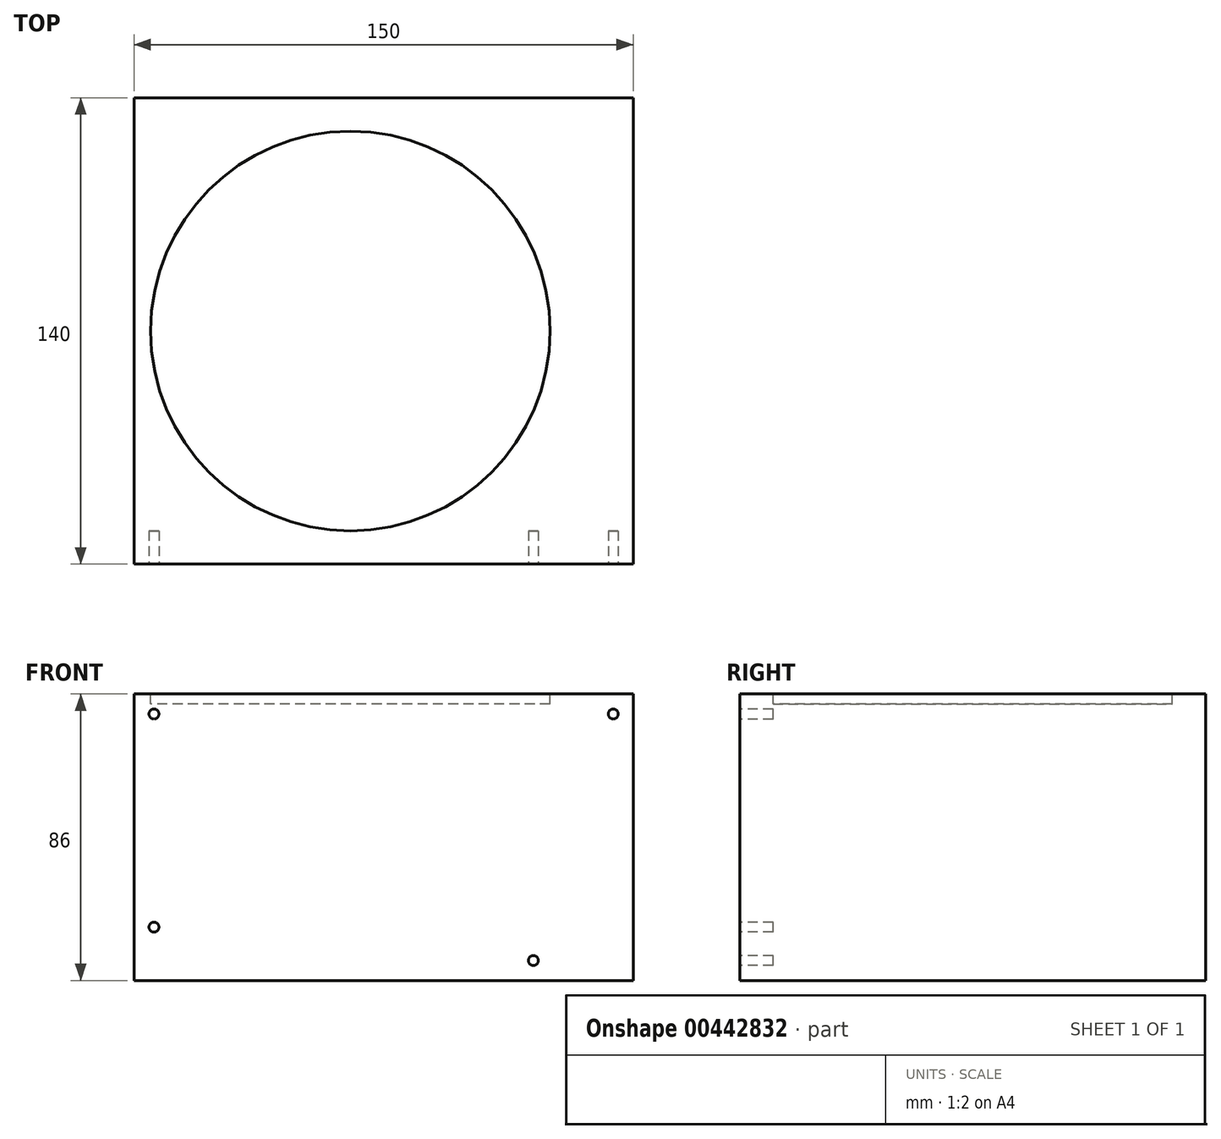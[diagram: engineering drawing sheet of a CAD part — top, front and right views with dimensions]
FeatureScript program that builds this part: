
annotation { "Feature Type Name" : "Feature", "Feature Type Description" : "" }
export const myFeature = defineFeature(function(context is Context, id is Id, definition is map)
    precondition{}
    {
        {
            var Q0;
            Q0=qCreatedBy(makeId("Top.planeOp"),FACE);
            var sketch = newSketch(context, id + "F0", { "sketchPlane" : qUnion([Q0])});
            skLineSegment(sketch, "E0.bottom", {"start": v(0, 0) * mm, "end": v(150, 0) * mm});
            skLineSegment(sketch, "E0.top", {"start": v(0, 140) * mm, "end": v(150, 140) * mm});
            skLineSegment(sketch, "E0.left", {"start": v(0, 0) * mm, "end": v(0, 140) * mm});
            skLineSegment(sketch, "E0.right", {"start": v(150, 0) * mm, "end": v(150, 140) * mm});
            skSolve(sketch);
        }
        {
            var Q0;
            Q0=qSketchRegion(id+"F0",true);
            extrude(context, id + "F1", {"entities" : qUnion([Q0]), "depth" : 86 * mm});
        }
        {
            var Q0;
            Q0=makeQuery(id+"F1.opExtrude","SWEPT_FACE",FACE,{"disambiguationData":[OSD([sQuery(id+"F0.wireOp",EDGE,"E0.bottom")])]});
            var sketch = newSketch(context, id + "F2", { "sketchPlane" : qUnion([Q0])});
            skCircle(sketch, "E1", {"center": v(6, 80) * mm, "radius": 1.5 * mm});
            skCircle(sketch, "E2", {"center": v(6, 16) * mm, "radius": 1.5 * mm});
            skCircle(sketch, "E3", {"center": v(144, 80) * mm, "radius": 1.5 * mm});
            skCircle(sketch, "E4", {"center": v(120, 6) * mm, "radius": 1.5 * mm});
            skSolve(sketch);
        }
        {
            var Q0;
            Q0=qSketchRegion(id+"F2",true);
            extrude(context, id + "F3", {"entities" : qUnion([Q0]), "operationType" : NewBodyOperationType.REMOVE, "oppositeDirection" : true, "depth" : 10 * mm});
        }
        {
            var Q0;
            Q0=makeQuery(id+"F1.opExtrude","CAP_FACE",FACE,{"disambiguationData":[OSD([sQuery(id+"F0.wireOp",EDGE,"E0.bottom"),sQuery(id+"F0.wireOp",EDGE,"E0.top"),sQuery(id+"F0.wireOp",EDGE,"E0.left"),sQuery(id+"F0.wireOp",EDGE,"E0.right")])],"isStart":false});
            var sketch = newSketch(context, id + "F4", { "sketchPlane" : qUnion([Q0])});
            skCircle(sketch, "E5", {"center": v(65, 70) * mm, "radius": 60 * mm});
            skSolve(sketch);
        }
        {
            var Q0;
            Q0=qSketchRegion(id+"F4",true);
            extrude(context, id + "F5", {"entities" : qUnion([Q0]), "operationType" : NewBodyOperationType.REMOVE, "oppositeDirection" : true, "depth" : 3 * mm});
        }
    });
